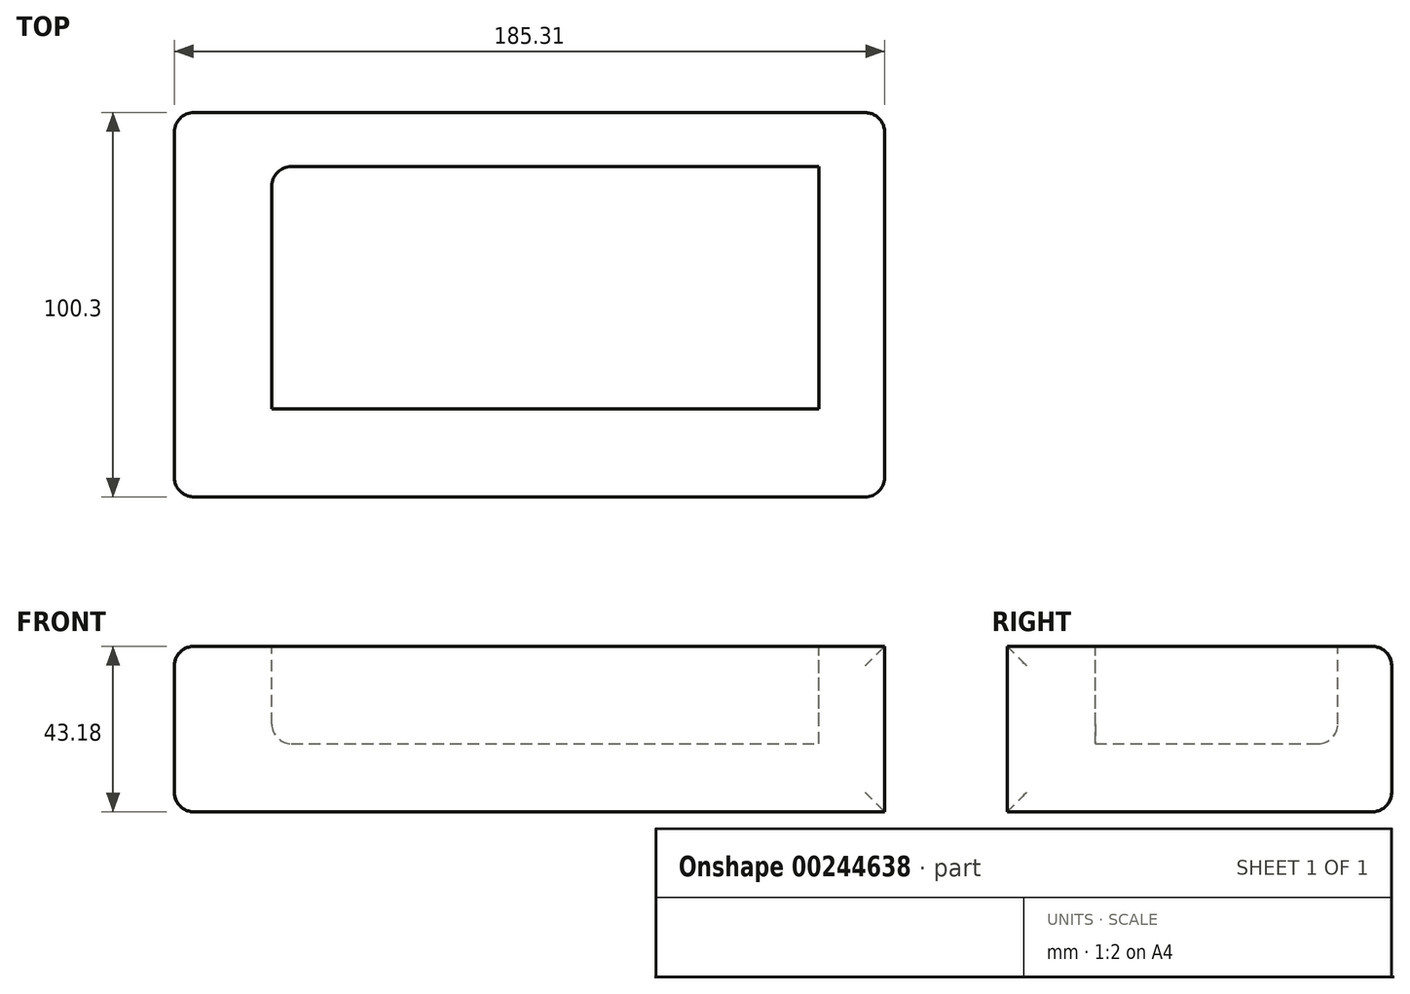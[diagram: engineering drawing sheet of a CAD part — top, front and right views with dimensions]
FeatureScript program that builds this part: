
annotation { "Feature Type Name" : "Feature", "Feature Type Description" : "" }
export const myFeature = defineFeature(function(context is Context, id is Id, definition is map)
    precondition{}
    {
        {
            var Q0;
            Q0=qCreatedBy(makeId("Top.planeOp"),FACE);
            var sketch = newSketch(context, id + "F0", { "sketchPlane" : qUnion([Q0])});
            skLineSegment(sketch, "E0.bottom", {"start": v(-82.39, -45.18) * mm, "end": v(102.92, -45.18) * mm});
            skLineSegment(sketch, "E0.top", {"start": v(-82.39, 55.12) * mm, "end": v(102.92, 55.12) * mm});
            skLineSegment(sketch, "E0.left", {"start": v(-82.39, -45.18) * mm, "end": v(-82.39, 55.12) * mm});
            skLineSegment(sketch, "E0.right", {"start": v(102.92, -45.18) * mm, "end": v(102.92, 55.12) * mm});
            skSolve(sketch);
        }
        {
            var Q0;
            Q0=makeQuery(id+"F0.imprint","IMPRINT",FACE,{"disambiguationData":[TD([[makeQuery(id+"F0.imprint","IMPRINT",EDGE,{"derivedFrom":sQuery(id+"F0.wireOp",EDGE,"E0.bottom")}),1.0]])]});
            extrude(context, id + "F1", {"entities" : qUnion([Q0]), "depth" : 43.18 * mm});
        }
        {
            var Q0;
            Q0=makeQuery(id+"F1.opExtrude","CAP_FACE",FACE,{"disambiguationData":[OSD([sQuery(id+"F0.wireOp",EDGE,"E0.bottom"),sQuery(id+"F0.wireOp",EDGE,"E0.top"),sQuery(id+"F0.wireOp",EDGE,"E0.left"),sQuery(id+"F0.wireOp",EDGE,"E0.right")])],"isStart":false});
            var sketch = newSketch(context, id + "F2", { "sketchPlane" : qUnion([Q0])});
            skLineSegment(sketch, "E1.bottom", {"start": v(-56.93, -22.23) * mm, "end": v(85.74, -22.23) * mm});
            skLineSegment(sketch, "E1.top", {"start": v(-56.93, 41.03) * mm, "end": v(85.74, 41.03) * mm});
            skLineSegment(sketch, "E1.left", {"start": v(-56.93, -22.23) * mm, "end": v(-56.93, 41.03) * mm});
            skLineSegment(sketch, "E1.right", {"start": v(85.74, -22.23) * mm, "end": v(85.74, 41.03) * mm});
            skSolve(sketch);
        }
        {
            var Q0;
            Q0=makeQuery(id+"F2.imprint","IMPRINT",FACE,{"disambiguationData":[TD([[makeQuery(id+"F2.imprint","IMPRINT",EDGE,{"derivedFrom":sQuery(id+"F2.wireOp",EDGE,"E1.bottom")}),1.0]])]});
            extrude(context, id + "F3", {"entities" : qUnion([Q0]), "operationType" : NewBodyOperationType.REMOVE, "oppositeDirection" : true, "depth" : 25.4 * mm});
        }
        {
            var Q0;
            Q0=makeQuery(id+"F1.opExtrude","SWEPT_EDGE",EDGE,{"disambiguationData":[OSD([sQuery(id+"F0.wireOp",EDGE,"E0.bottom"),sQuery(id+"F0.wireOp",EDGE,"E0.left")])]});
            var Q1;
            Q1=makeQuery(id+"F1.opExtrude","SWEPT_EDGE",EDGE,{"disambiguationData":[OSD([sQuery(id+"F0.wireOp",EDGE,"E0.bottom"),sQuery(id+"F0.wireOp",EDGE,"E0.right")])]});
            var Q2;
            Q2=makeQuery(id+"F1.opExtrude","SWEPT_EDGE",EDGE,{"disambiguationData":[OSD([sQuery(id+"F0.wireOp",EDGE,"E0.top"),sQuery(id+"F0.wireOp",EDGE,"E0.right")])]});
            var Q3;
            Q3=makeQuery(id+"F1.opExtrude","CAP_EDGE",EDGE,{"disambiguationData":[OSD([sQuery(id+"F0.wireOp",EDGE,"E0.top")])],"isStart":false});
            var Q4;
            Q4=makeQuery(id+"F3.boolean.opBoolean","COPY",EDGE,{"derivedFrom":makeQuery(id+"F3.opExtrude","CAP_EDGE",EDGE,{"disambiguationData":[OSD([sQuery(id+"F2.wireOp",EDGE,"E1.top")])],"isStart":true})});
            var Q5;
            Q5=makeQuery(id+"F1.opExtrude","SWEPT_EDGE",EDGE,{"disambiguationData":[OSD([sQuery(id+"F0.wireOp",EDGE,"E0.top"),sQuery(id+"F0.wireOp",EDGE,"E0.left")])]});
            var Q6;
            Q6=makeQuery(id+"F3.boolean.opBoolean","COPY",EDGE,{"derivedFrom":makeQuery(id+"F3.opExtrude","SWEPT_EDGE",EDGE,{"disambiguationData":[OSD([sQuery(id+"F2.wireOp",EDGE,"E1.top"),sQuery(id+"F2.wireOp",EDGE,"E1.left")])]})});
            var Q7;
            Q7=makeQuery(id+"F3.boolean.opBoolean","COPY",EDGE,{"derivedFrom":makeQuery(id+"F3.opExtrude","CAP_EDGE",EDGE,{"disambiguationData":[OSD([sQuery(id+"F2.wireOp",EDGE,"E1.bottom")])],"isStart":true})});
            var Q8;
            Q8=makeQuery(id+"F3.boolean.opBoolean","COPY",EDGE,{"derivedFrom":makeQuery(id+"F3.opExtrude","CAP_EDGE",EDGE,{"disambiguationData":[OSD([sQuery(id+"F2.wireOp",EDGE,"E1.top")])],"isStart":false})});
            var Q9;
            Q9=makeQuery(id+"F3.boolean.opBoolean","COPY",EDGE,{"derivedFrom":makeQuery(id+"F3.opExtrude","CAP_EDGE",EDGE,{"disambiguationData":[OSD([sQuery(id+"F2.wireOp",EDGE,"E1.left")])],"isStart":true})});
            var Q10;
            Q10=makeQuery(id+"F3.boolean.opBoolean","COPY",EDGE,{"derivedFrom":makeQuery(id+"F3.opExtrude","CAP_EDGE",EDGE,{"disambiguationData":[OSD([sQuery(id+"F2.wireOp",EDGE,"E1.left")])],"isStart":false})});
            var Q11;
            Q11=makeQuery(id+"F1.opExtrude","CAP_EDGE",EDGE,{"disambiguationData":[OSD([sQuery(id+"F0.wireOp",EDGE,"E0.top")])],"isStart":true});
            var Q12;
            Q12=makeQuery(id+"F1.opExtrude","CAP_EDGE",EDGE,{"disambiguationData":[OSD([sQuery(id+"F0.wireOp",EDGE,"E0.left")])],"isStart":false});
            var Q13;
            Q13=makeQuery(id+"F1.opExtrude","CAP_EDGE",EDGE,{"disambiguationData":[OSD([sQuery(id+"F0.wireOp",EDGE,"E0.left")])],"isStart":true});
            fillet(context, id + "F4", {"entities" : qUnion([Q0, Q1, Q2, Q3, Q4, Q5, Q6, Q7, Q8, Q9, Q10, Q11, Q12, Q13]), "radius" : 5.08 * mm, "tangentPropagation" : true, "allowEdgeOverflow" : false});
        }
    });
